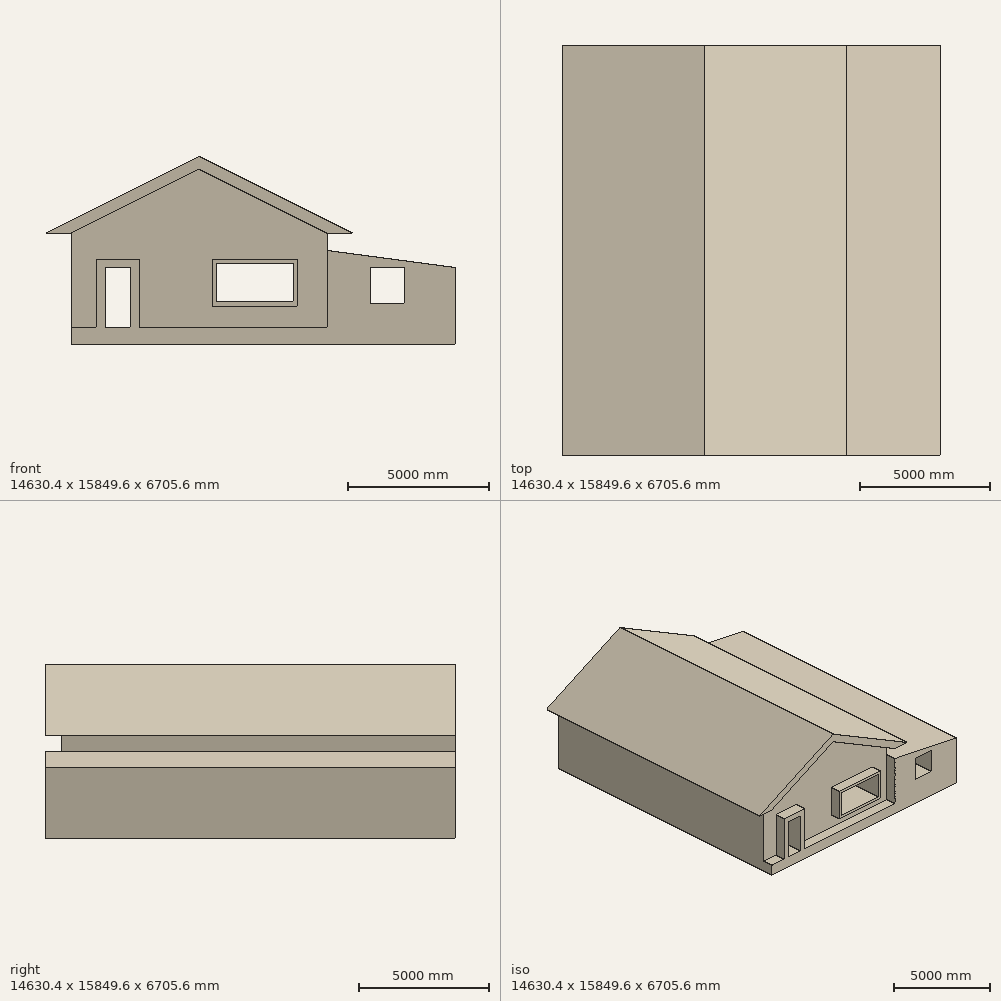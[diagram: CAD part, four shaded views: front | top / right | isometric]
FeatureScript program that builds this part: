
annotation { "Feature Type Name" : "Feature", "Feature Type Description" : "" }
export const myFeature = defineFeature(function(context is Context, id is Id, definition is map)
    precondition{}
    {
        {
            var Q0;
            Q0=qCreatedBy(makeId("Front.planeOp"),FACE);
            var sketch = newSketch(context, id + "F0", { "sketchPlane" : qUnion([Q0])});
            skLineSegment(sketch, "E0", {"start": v(0, 0) * mm, "end": v(-4572, 0) * mm});
            skLineSegment(sketch, "E1", {"start": v(0, 0) * mm, "end": v(4572, 0) * mm});
            skLineSegment(sketch, "E2", {"start": v(0, 0) * mm, "end": v(0, 2286) * mm});
            skLineSegment(sketch, "E3", {"start": v(0, 2286) * mm, "end": v(-4572, 0) * mm});
            skLineSegment(sketch, "E4", {"start": v(0, 2286) * mm, "end": v(4572, 0) * mm});
            skLineSegment(sketch, "E5", {"start": v(0, 2286) * mm, "end": v(0, 2743.2) * mm});
            skLineSegment(sketch, "E6", {"start": v(0, 2743.2) * mm, "end": v(-5486.4, 0) * mm});
            skLineSegment(sketch, "E7", {"start": v(-5486.4, 0) * mm, "end": v(-4572, 0) * mm});
            skLineSegment(sketch, "E8", {"start": v(0, 2743.2) * mm, "end": v(5486.4, 0) * mm});
            skLineSegment(sketch, "E9", {"start": v(5486.4, 0) * mm, "end": v(4572, 0) * mm});
            skLineSegment(sketch, "E10", {"start": v(-4572, 0) * mm, "end": v(-4572, -3352.8) * mm});
            skLineSegment(sketch, "E11", {"start": v(4572, 0) * mm, "end": v(4572, -3352.8) * mm});
            skLineSegment(sketch, "E12", {"start": v(4572, -3352.8) * mm, "end": v(-4572, -3352.8) * mm});
            skLineSegment(sketch, "E13", {"start": v(-4572, -3352.8) * mm, "end": v(-4572, -3962.4) * mm});
            skLineSegment(sketch, "E14", {"start": v(4572, -3352.8) * mm, "end": v(4572, -3962.4) * mm});
            skLineSegment(sketch, "E15", {"start": v(4572, -3962.4) * mm, "end": v(-4572, -3962.4) * mm});
            skLineSegment(sketch, "E16.bottom", {"start": v(609.6, -1074.5) * mm, "end": v(3352.8, -1074.5) * mm});
            skLineSegment(sketch, "E16.top", {"start": v(609.6, -2446.1) * mm, "end": v(3352.8, -2446.1) * mm});
            skLineSegment(sketch, "E16.left", {"start": v(609.6, -1074.5) * mm, "end": v(609.6, -2446.1) * mm});
            skLineSegment(sketch, "E16.right", {"start": v(3352.8, -1074.5) * mm, "end": v(3352.8, -2446.1) * mm});
            skLineSegment(sketch, "E17.0", {"start": v(457.2, -922.1) * mm, "end": v(3505.2, -922.1) * mm});
            skLineSegment(sketch, "E17.1", {"start": v(457.2, -922.1) * mm, "end": v(457.2, -2598.5) * mm});
            skLineSegment(sketch, "E17.2", {"start": v(457.2, -2598.5) * mm, "end": v(3505.2, -2598.5) * mm});
            skLineSegment(sketch, "E17.3", {"start": v(3505.2, -922.1) * mm, "end": v(3505.2, -2598.5) * mm});
            skLineSegment(sketch, "E18", {"start": v(-3352.8, -3352.8) * mm, "end": v(-3352.8, -1219.2) * mm});
            skLineSegment(sketch, "E19", {"start": v(-2438.4, -1219.2) * mm, "end": v(-2438.4, -3352.8) * mm});
            skLineSegment(sketch, "E20", {"start": v(-3352.8, -1219.2) * mm, "end": v(-2438.4, -1219.2) * mm});
            skLineSegment(sketch, "E21.0", {"start": v(-2133.6, -914.4) * mm, "end": v(-2133.6, -3352.8) * mm});
            skLineSegment(sketch, "E21.1", {"start": v(-3657.6, -914.4) * mm, "end": v(-2133.6, -914.4) * mm});
            skLineSegment(sketch, "E21.2", {"start": v(-3657.6, -3352.8) * mm, "end": v(-3657.6, -914.4) * mm});
            skLineSegment(sketch, "E22", {"start": v(4572, -3352.8) * mm, "end": v(9144, -3352.8) * mm});
            skLineSegment(sketch, "E23", {"start": v(9144, -3352.8) * mm, "end": v(9144, -609.6) * mm});
            skLineSegment(sketch, "E24", {"start": v(9144, -609.6) * mm, "end": v(4572, 0) * mm});
            skLineSegment(sketch, "E25", {"start": v(4572, -609.6) * mm, "end": v(9144, -1219.2) * mm});
            skLineSegment(sketch, "E26", {"start": v(4572, -3962.4) * mm, "end": v(9144, -3962.4) * mm});
            skLineSegment(sketch, "E27", {"start": v(9144, -3962.4) * mm, "end": v(9144, -3352.8) * mm});
            skLineSegment(sketch, "E28.bottom", {"start": v(6096, -1215.64) * mm, "end": v(7315.2, -1215.64) * mm});
            skLineSegment(sketch, "E28.top", {"start": v(6096, -2506.78) * mm, "end": v(7315.2, -2506.78) * mm});
            skLineSegment(sketch, "E28.left", {"start": v(6096, -1215.64) * mm, "end": v(6096, -2506.78) * mm});
            skLineSegment(sketch, "E28.right", {"start": v(7315.2, -1215.64) * mm, "end": v(7315.2, -2506.78) * mm});
            skLineSegment(sketch, "E29.0", {"start": v(6248.4, -1368.04) * mm, "end": v(7162.8, -1368.04) * mm});
            skLineSegment(sketch, "E29.1", {"start": v(6248.4, -1368.04) * mm, "end": v(6248.4, -2354.38) * mm});
            skLineSegment(sketch, "E29.2", {"start": v(6248.4, -2354.38) * mm, "end": v(7162.8, -2354.38) * mm});
            skLineSegment(sketch, "E29.3", {"start": v(7162.8, -1368.04) * mm, "end": v(7162.8, -2354.38) * mm});
            skText(sketch, "E30", { "text": "Sophia", "fontName": "AllertaStencil-Regular.ttf"});
            const initialGuessF0  = {"E30": [-3.3263, 4.0466, 1, 0, 0.64553]};
            skSetInitialGuess(sketch, initialGuessF0);
            skSolve(sketch);
        }
        {
            var Q0;
            Q0=makeQuery(id+"F0.imprint","IMPRINT",FACE,{"disambiguationData":[TD([[makeQuery(id+"F0.imprint","IMPRINT",EDGE,{"derivedFrom":sQuery(id+"F0.wireOp",EDGE,"E0")}),1.0]])]});
            var Q1;
            Q1=makeQuery(id+"F0.imprint","IMPRINT",FACE,{"disambiguationData":[TD([[makeQuery(id+"F0.imprint","IMPRINT",EDGE,{"derivedFrom":sQuery(id+"F0.wireOp",EDGE,"E0")}),-1.0]])]});
            var Q2;
            Q2=makeQuery(id+"F0.imprint","IMPRINT",FACE,{"disambiguationData":[TD([[makeQuery(id+"F0.imprint","IMPRINT",EDGE,{"derivedFrom":sQuery(id+"F0.wireOp",EDGE,"E1")}),1.0]])]});
            var Q3;
            {var subQ2=sQuery(id+"F0.wireOp",EDGE,"E22");Q3=makeQuery(id+"F0.imprint","IMPRINT",FACE,{"disambiguationData":[TD([[makeQuery(id+"F0.imprint","IMPRINT",EDGE,{"derivedFrom":subQ2}),1.0]])]});}
            extrude(context, id + "F1", {"entities" : qUnion([Q0, Q1, Q2, Q3]), "depth" : 15240 * mm, "offsetDistance" : 30.48 * mm});
        }
        {
            var Q0;
            Q0=makeQuery(id+"F0.imprint","IMPRINT",FACE,{"disambiguationData":[TD([[makeQuery(id+"F0.imprint","IMPRINT",EDGE,{"derivedFrom":sQuery(id+"F0.wireOp",EDGE,"E4")}),1.0]])]});
            var Q1;
            Q1=makeQuery(id+"F0.imprint","IMPRINT",FACE,{"disambiguationData":[TD([[makeQuery(id+"F0.imprint","IMPRINT",EDGE,{"derivedFrom":sQuery(id+"F0.wireOp",EDGE,"E3")}),-1.0]])]});
            var Q2;
            Q2=makeQuery(id+"F0.imprint","IMPRINT",FACE,{"disambiguationData":[TD([[makeQuery(id+"F0.imprint","IMPRINT",EDGE,{"derivedFrom":sQuery(id+"F0.wireOp",EDGE,"E16.bottom")}),1.0]])]});
            var Q3;
            {var subQ1=sQuery(id+"F0.wireOp",EDGE,"E18");Q3=makeQuery(id+"F0.imprint","IMPRINT",FACE,{"disambiguationData":[TD([[makeQuery(id+"F0.imprint","IMPRINT",EDGE,{"derivedFrom":subQ1}),1.0]])]});}
            var Q4;
            {var subQ2=sQuery(id+"F0.wireOp",EDGE,"E22");Q4=makeQuery(id+"F0.imprint","IMPRINT",FACE,{"disambiguationData":[TD([[makeQuery(id+"F0.imprint","IMPRINT",EDGE,{"derivedFrom":subQ2}),1.0]])]});}
            var Q5;
            Q5=makeQuery(id+"F0.imprint","IMPRINT",FACE,{"disambiguationData":[TD([[makeQuery(id+"F0.imprint","IMPRINT",EDGE,{"derivedFrom":sQuery(id+"F0.wireOp",EDGE,"E14")}),1.0]])]});
            var Q6;
            {var subQ6=sQuery(id+"F0.wireOp",EDGE,"E13");Q6=makeQuery(id+"F0.imprint","IMPRINT",FACE,{"disambiguationData":[TD([[makeQuery(id+"F0.imprint","IMPRINT",EDGE,{"derivedFrom":subQ6}),1.0]])]});}
            extrude(context, id + "F2", {"entities" : qUnion([Q0, Q1, Q2, Q3, Q4, Q5, Q6]), "operationType" : NewBodyOperationType.ADD, "depth" : 15849.6 * mm, "offsetDistance" : 30.48 * mm});
        }
    });
